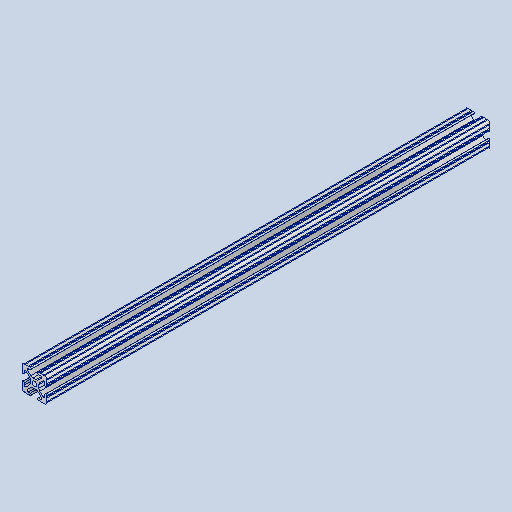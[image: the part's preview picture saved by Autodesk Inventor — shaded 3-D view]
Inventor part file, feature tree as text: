
AUTODESK INVENTOR PART (.ipt)
format: ipt  version: 2023 (Build 270158000, 158)  size: 341,504 bytes
history: native  units: in
note: dims shown in document units (in); Inventor stores cm internally (conversion verified against a paired STEP export)
features: extrude x1, sketch x1, projected_geometry x1, other x1
ambient origin geometry x8: Origin, YZ Plane, XZ Plane, XY Plane, X Axis, Y Axis, Z Axis, Center Point
bodies: Solid1 (feature_tree)
feature tree (4):
  extrude  "Extrusion1"  [1 undecoded]
  sketch  "Sketch1"  dims[d0=6.0in d1=0.0in]
  projected_geometry  "Projected Loop1"
  other  "Boss-Extrude1"
note: 1 required parameter value undecoded (feature->parameter linkage not recoverable at this tier; creation-order binding heuristic only, values carry confidence <= 0.55)
